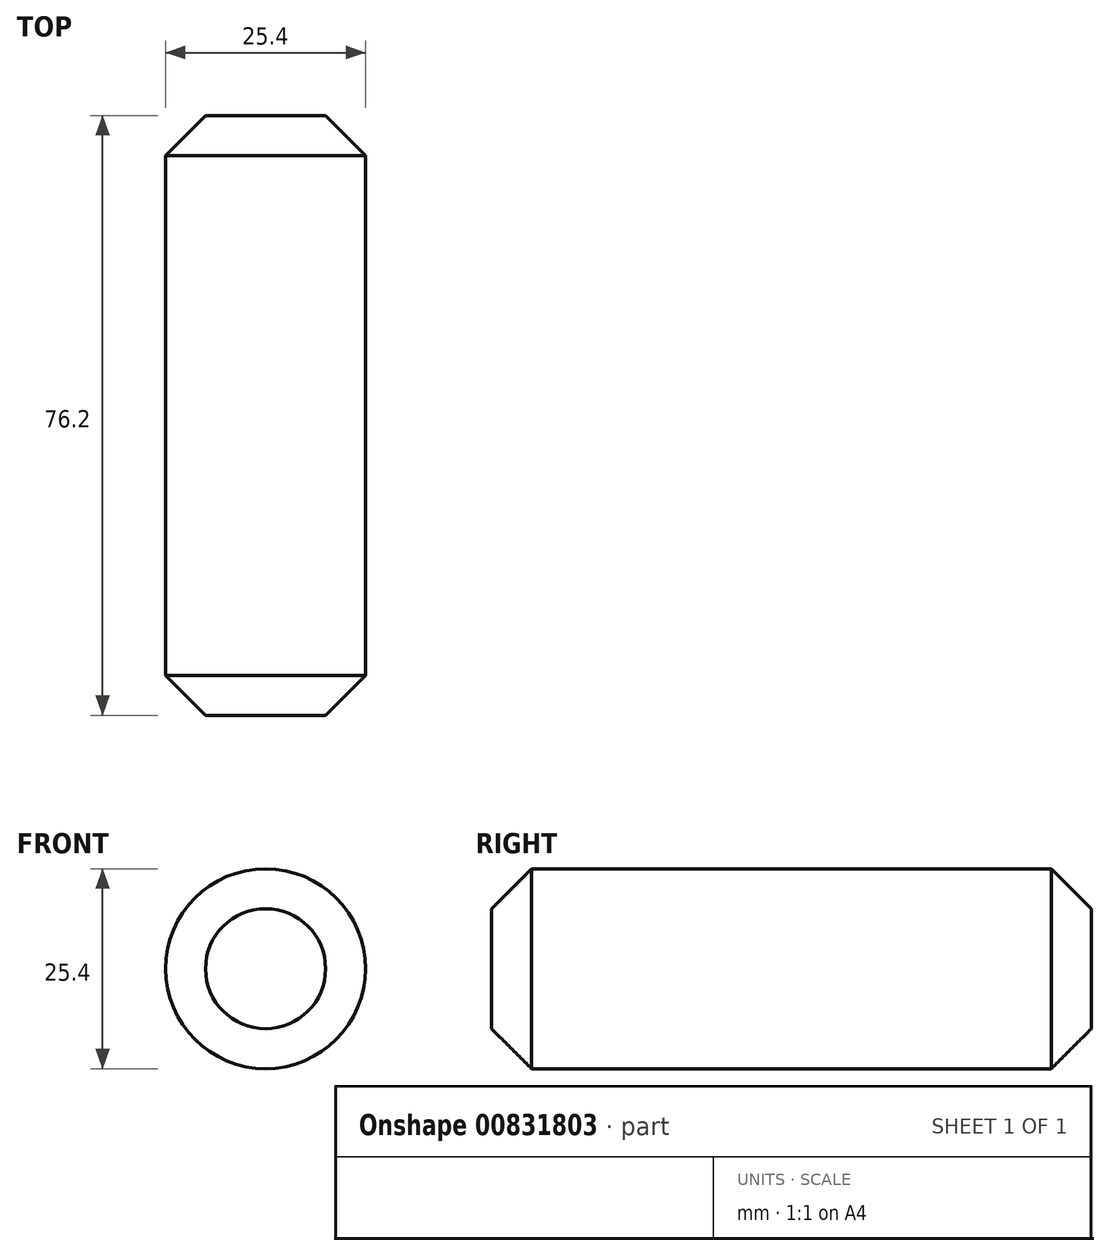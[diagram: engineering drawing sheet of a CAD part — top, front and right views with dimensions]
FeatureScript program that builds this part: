
annotation { "Feature Type Name" : "Feature", "Feature Type Description" : "" }
export const myFeature = defineFeature(function(context is Context, id is Id, definition is map)
    precondition{}
    {
        {
            var Q0;
            Q0=qCreatedBy(makeId("Front.planeOp"),FACE);
            var sketch = newSketch(context, id + "F0", { "sketchPlane" : qUnion([Q0])});
            skCircle(sketch, "E0", {"center": v(0, 0) * mm, "radius": 12.7 * mm});
            skCircle(sketch, "E1", {"center": v(0, 0) * mm, "radius": 5.08 * mm});
            skSolve(sketch);
        }
        {
            var Q0;
            Q0=makeQuery(id+"F0.imprint","IMPRINT",FACE,{"disambiguationData":[TD([[makeQuery(id+"F0.imprint","IMPRINT",EDGE,{"derivedFrom":sQuery(id+"F0.wireOp",EDGE,"E0")}),1.0]])]});
            extrude(context, id + "F1", {"entities" : qUnion([Q0]), "depth" : 76.2 * mm, "offsetDistance" : 25.4 * mm});
        }
        {
            var Q0;
            Q0=makeQuery(id+"F0.imprint","IMPRINT",FACE,{"disambiguationData":[TD([[makeQuery(id+"F0.imprint","IMPRINT",EDGE,{"derivedFrom":sQuery(id+"F0.wireOp",EDGE,"E1")}),1.0]])]});
            extrude(context, id + "F2", {"entities" : qUnion([Q0]), "operationType" : NewBodyOperationType.ADD, "depth" : 76.2 * mm, "offsetDistance" : 25.4 * mm});
        }
        {
            var Q0;
            Q0=makeQuery(id+"F1.opExtrude","CAP_EDGE",EDGE,{"disambiguationData":[OSD([sQuery(id+"F0.wireOp",EDGE,"E0")])],"isStart":false});
            var Q1;
            Q1=makeQuery(id+"F1.opExtrude","CAP_EDGE",EDGE,{"disambiguationData":[OSD([sQuery(id+"F0.wireOp",EDGE,"E0")])],"isStart":true});
            chamfer(context, id + "F3", {"entities" : qUnion([Q0, Q1]), "width" : 5.08 * mm, "tangentPropagation" : true});
        }
    });
